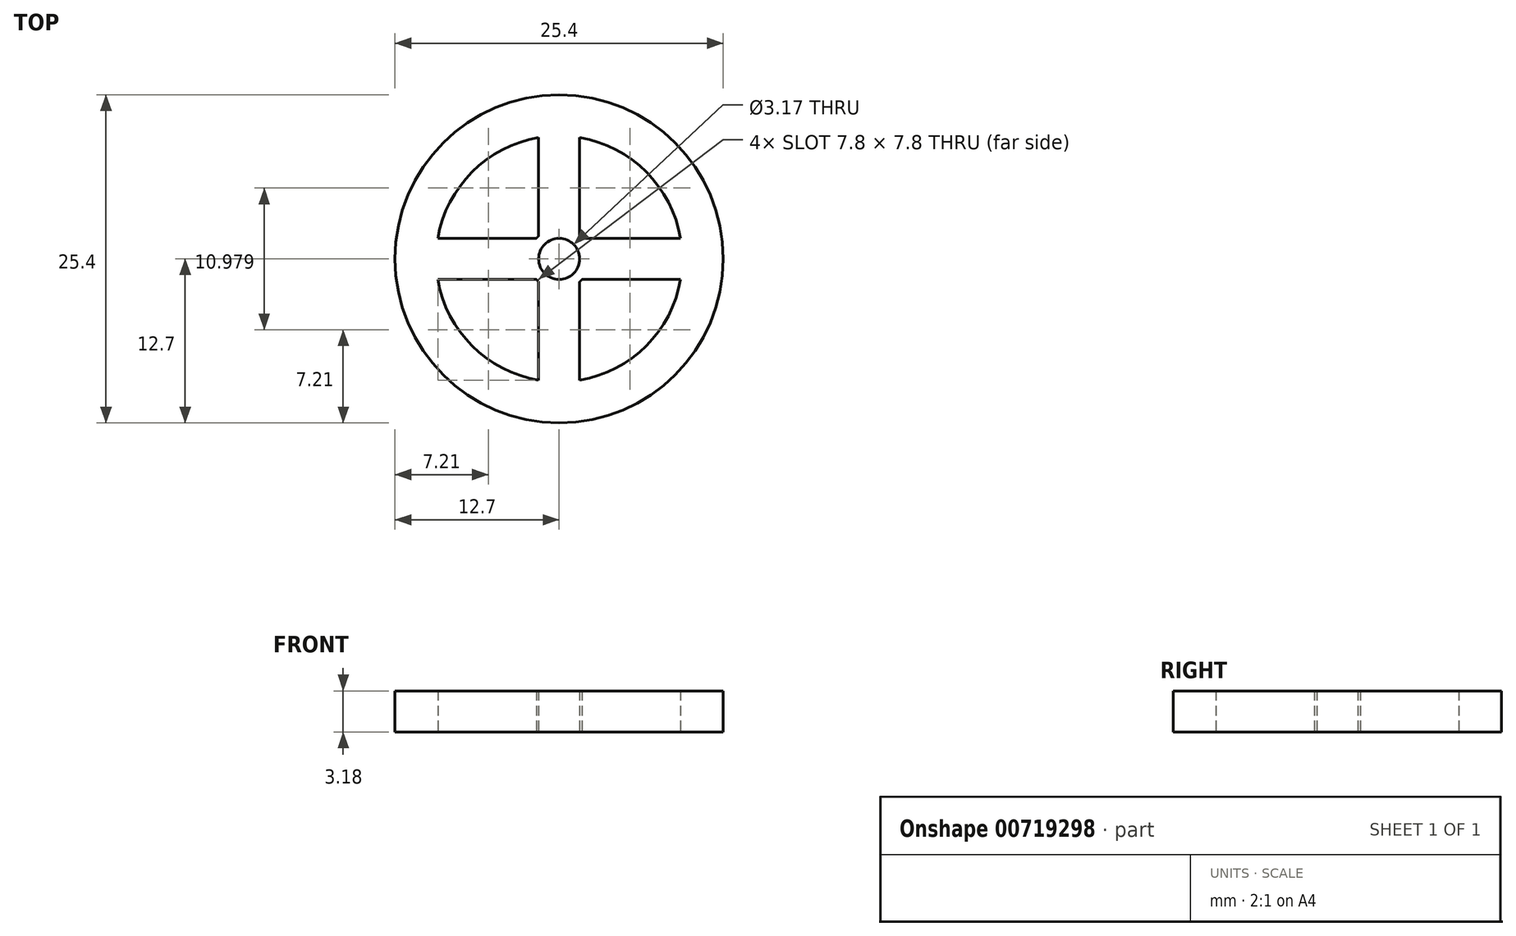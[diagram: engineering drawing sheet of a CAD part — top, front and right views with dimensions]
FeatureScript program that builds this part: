
annotation { "Feature Type Name" : "Feature", "Feature Type Description" : "" }
export const myFeature = defineFeature(function(context is Context, id is Id, definition is map)
    precondition{}
    {
        {
            var Q0;
            Q0=qCreatedBy(makeId("Top.planeOp"),FACE);
            var sketch = newSketch(context, id + "F0", { "sketchPlane" : qUnion([Q0])});
            skCircle(sketch, "E0", {"center": v(0, 0) * mm, "radius": 12.7 * mm});
            skArc(sketch, "E1", {"start": v(-9.4, -1.59) * mm, "mid": v(-6.74, -6.74) * mm, "end": v(-1.59, -9.4) * mm});
            skArc(sketch, "E2", {"start": v(1.59, -1.77) * mm, "mid": v(1.68, -1.68) * mm, "end": v(1.77, -1.59) * mm});
            skCircle(sketch, "E3", {"center": v(0, 0) * mm, "radius": 1.59 * mm});
            skLineSegment(sketch, "E4", {"start": v(0, 0) * mm, "end": v(0, 9.53) * mm, "construction": true});
            skLineSegment(sketch, "E5", {"start": v(0, 0) * mm, "end": v(-9.53, 0) * mm, "construction": true});
            skLineSegment(sketch, "E6", {"start": v(0, 0) * mm, "end": v(0, -9.53) * mm, "construction": true});
            skLineSegment(sketch, "E7", {"start": v(0, 0) * mm, "end": v(9.53, 0) * mm, "construction": true});
            skLineSegment(sketch, "E8.0", {"start": v(1.59, 1.77) * mm, "end": v(1.59, 9.4) * mm});
            skLineSegment(sketch, "E9.0", {"start": v(-1.59, 1.77) * mm, "end": v(-1.59, 9.4) * mm});
            skLineSegment(sketch, "E10.0", {"start": v(-1.77, 1.59) * mm, "end": v(-9.4, 1.59) * mm});
            skLineSegment(sketch, "E11.0", {"start": v(-1.77, -1.59) * mm, "end": v(-9.4, -1.59) * mm});
            skLineSegment(sketch, "E12.0", {"start": v(-1.59, -1.77) * mm, "end": v(-1.59, -9.4) * mm});
            skLineSegment(sketch, "E13.0", {"start": v(1.59, -1.77) * mm, "end": v(1.59, -9.4) * mm});
            skLineSegment(sketch, "E14.0", {"start": v(1.77, 1.59) * mm, "end": v(9.4, 1.59) * mm});
            skLineSegment(sketch, "E15.0", {"start": v(1.77, -1.59) * mm, "end": v(9.4, -1.59) * mm});
            skArc(sketch, "E16.trimOffspring", {"start": v(1.59, -9.4) * mm, "mid": v(6.74, -6.74) * mm, "end": v(9.4, -1.59) * mm});
            skArc(sketch, "E17.trimOffspring", {"start": v(9.4, 1.59) * mm, "mid": v(6.74, 6.74) * mm, "end": v(1.59, 9.4) * mm});
            skArc(sketch, "E18.trimOffspring", {"start": v(-1.59, 9.4) * mm, "mid": v(-6.74, 6.74) * mm, "end": v(-9.4, 1.59) * mm});
            skArc(sketch, "E19.trimOffspring", {"start": v(-1.77, -1.59) * mm, "mid": v(-1.68, -1.68) * mm, "end": v(-1.59, -1.77) * mm});
            skArc(sketch, "E20.trimOffspring", {"start": v(-1.59, 1.77) * mm, "mid": v(-1.68, 1.68) * mm, "end": v(-1.77, 1.59) * mm});
            skArc(sketch, "E21.trimOffspring", {"start": v(1.77, 1.59) * mm, "mid": v(1.68, 1.68) * mm, "end": v(1.59, 1.77) * mm});
            skSolve(sketch);
        }
        {
            var Q0;
            Q0=makeQuery(id+"F0.imprint","IMPRINT",FACE,{"disambiguationData":[TD([[makeQuery(id+"F0.imprint","IMPRINT",EDGE,{"derivedFrom":sQuery(id+"F0.wireOp",EDGE,"E0")}),1.0]])]});
            extrude(context, id + "F1", {"entities" : qUnion([Q0]), "depth" : 3.17 * mm, "offsetDistance" : 25.4 * mm});
        }
    });
